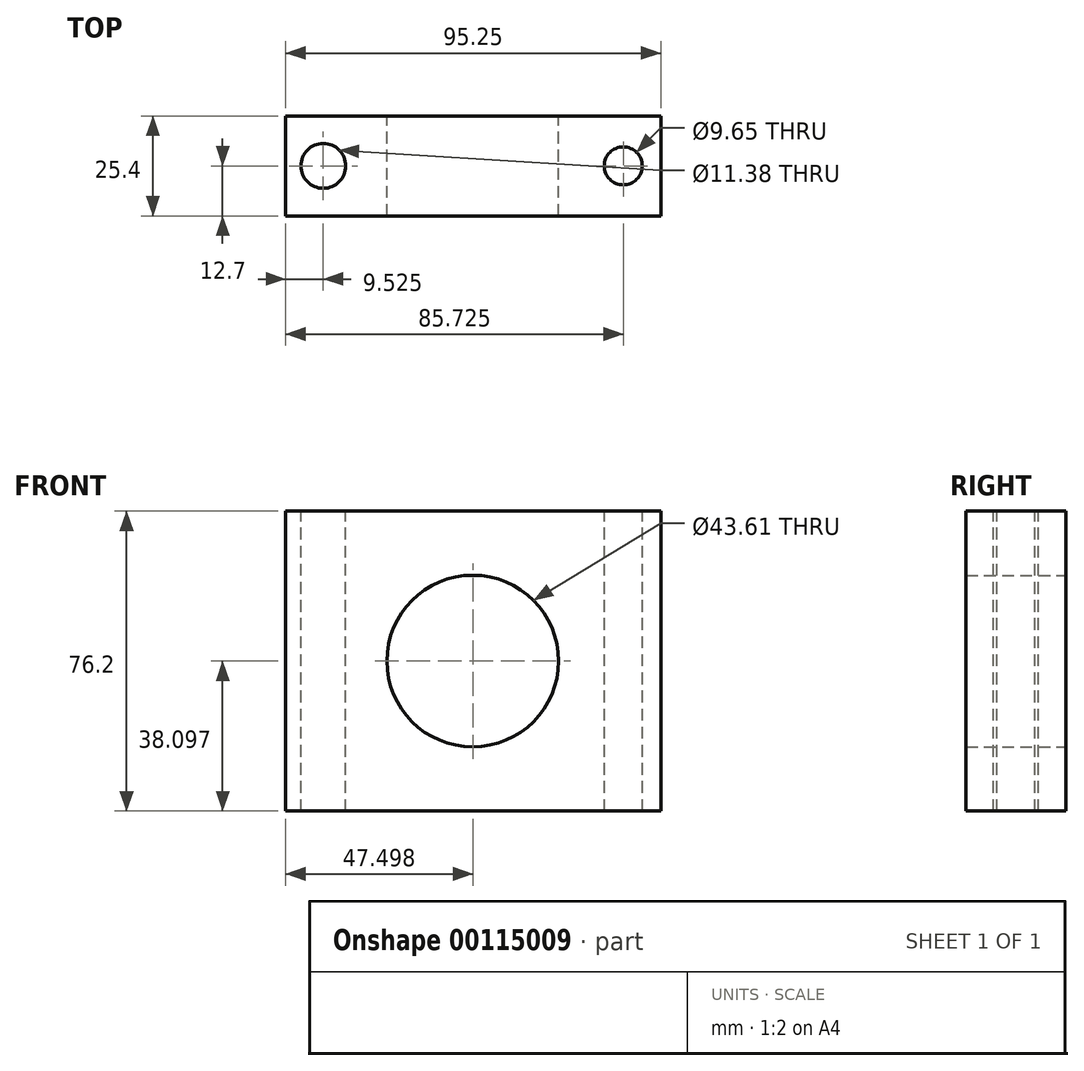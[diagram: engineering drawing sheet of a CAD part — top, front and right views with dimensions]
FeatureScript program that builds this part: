
annotation { "Feature Type Name" : "Feature", "Feature Type Description" : "" }
export const myFeature = defineFeature(function(context is Context, id is Id, definition is map)
    precondition{}
    {
        {
            var Q0;
            Q0=qCreatedBy(makeId("Front.planeOp"),FACE);
            var sketch = newSketch(context, id + "F0", { "sketchPlane" : qUnion([Q0])});
            skLineSegment(sketch, "E0", {"start": v(-39.87, 44.93) * mm, "end": v(55.38, 44.93) * mm});
            skLineSegment(sketch, "E1", {"start": v(55.38, 44.93) * mm, "end": v(55.38, -31.27) * mm});
            skLineSegment(sketch, "E2", {"start": v(55.38, -31.27) * mm, "end": v(-39.87, -31.27) * mm});
            skLineSegment(sketch, "E3", {"start": v(-39.87, -31.27) * mm, "end": v(-39.87, 44.93) * mm});
            skCircle(sketch, "E4", {"center": v(7.63, 6.83) * mm, "radius": 21.8 * mm});
            skSolve(sketch);
        }
        {
            var Q0;
            Q0 = qSketchRegion(id + "F0", true);
            extrude(context, id + "F1", {"entities" : qUnion([Q0]), "depth" : 25.4 * mm});
        }
        {
            var Q0;
            Q0=makeQuery(id+"F1.opExtrude","SWEPT_FACE",FACE,{"disambiguationData":[OSD([sQuery(id+"F0.wireOp",EDGE,"E0")])]});
            var sketch = newSketch(context, id + "F2", { "sketchPlane" : qUnion([Q0])});
            skCircle(sketch, "E5", {"center": v(-30.34, -12.7) * mm, "radius": 5.7 * mm});
            skPoint(sketch, "E5.centerSnap0", {"position": v(-39.87, -12.7) * mm});
            skCircle(sketch, "E6", {"center": v(45.86, -12.7) * mm, "radius": 4.83 * mm});
            skPoint(sketch, "E6.centerSnap0", {"position": v(55.38, -12.7) * mm});
            skSolve(sketch);
        }
        {
            var Q0;
            Q0 = qSketchRegion(id + "F2", true);
            extrude(context, id + "F3", {"entities" : qUnion([Q0]), "operationType" : NewBodyOperationType.REMOVE, "oppositeDirection" : true, "depth" : 80.52 * mm});
        }
    });
